# Revit family: DC_Holyoake_AirfoilControlDamper_HCD-75-FPL_13
name_source: partatom
category: Air Terminals
revit_build: Autodesk Revit 2014 (Build: 20130308_1515(x64)
units: mm (PartAtom-declared; Revit-internal decimal feet)

## types (1)
- HCD-75-FPL
    Air Stream Height = 500 mm  [stored 1.64042 ft]
    Air Stream Width = 600 mm  [stored 1.9685 ft]
    Blade Angle = Actural axle placement may vary
    Blade Count = 6
    Blade Pitch = 73 mm
    Damper Depth = 113 mm  [stored 0.370735 ft]
    Exact Overall Flange Height = 550 mm
    Exact Overall Flange Width = 650 mm  [stored 2.13255 ft]
    Flange Width = 25 mm  [stored 0.082021 ft]
    Louvre Offset = 500 mm  [stored 1.64042 ft]
    Manufacturer = Holyoake Industries Ltd
    Max Flow = 1000.0 L/s
    Maximum Size = 950mm wide and 898mm high (Air Stream)
    Min Flow = 100.0 L/s
    Minimun Size = 150mm wide and 95mm high (Air Stream)
    Model = HCD-75-FPL
    Static Pressure Max = 0.0 Pa
    Static Pressure Min = 0.0 Pa
    Technical Data = http://www.productspec.net
    Type Comments = Airfoil Control Damper
    URL = http://www.productspec.net

note: [stored X ft] marks values corroborated as IEEE doubles in the binary element streams (Revit-internal decimal feet)

## geometry (parser evidence)
native form markers: Blend x6, Sweep x6
no freeform markers — native parametric forms only
